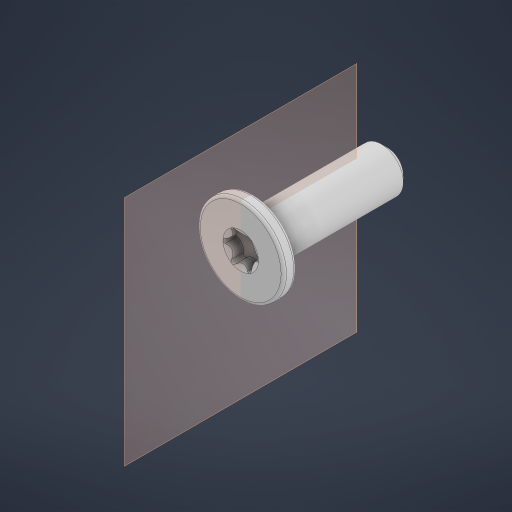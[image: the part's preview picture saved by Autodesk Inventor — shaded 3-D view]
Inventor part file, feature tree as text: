
AUTODESK INVENTOR PART (.ipt)
format: ipt  version: 2024.2 (Build 282272000, 272)  size: 308,224 bytes
history: native  units: in
note: dims shown in document units (in); Inventor stores cm internally (conversion verified against a paired STEP export)
features: other x18, sketch x6, extrude x3, fillet x1, chamfer x1, plane x1, revolve x1
ambient origin geometry x8: Origin, YZ Plane, XZ Plane, XY Plane, X Axis, Y Axis, Z Axis, Center Point
bodies: Solid1 (feature_tree)
feature tree (31):
  other  "Table"
  other  "Screw Steel Flat Head - Star"
  other  "SScrew Star Flat-Head 0.290"
  other  "SScrew Star Flat-Head 0.375"
  other  "SScrew Star Flat-Head 0.500"
  other  "SScrew Star Flat-Head 0.625"
  other  "SScrew Star Flat-Head 0.750"
  other  "SScrew Star Flat-Head 0.875"
  other  "SScrew Star Flat-Head 1.000"
  other  "SScrew Star Flat-Head 1.250"
  other  "SScrew Star Flat-Head 1.375"
  other  "SScrew Star Flat-Head 1.500"
  other  "SScrew Star Flat-Head 1.625"
  other  "SScrew Star Flat-Head 1.750"
  other  "SScrew Star Flat-Head 1.875"
  other  "SScrew Star Flat-Head 2.000"
  other  "SScrew Star Flat-Head 2.250"
  other  "SScrew Star Flat-Head 2.500"
  extrude  "Extrusion1"  Depth=0.047in TaperAngle=0.0deg
  fillet  "Fillet2"  Radius=0.01in
  extrude  "Extrusion2"  TaperAngle=60.0deg  [1 undecoded]
  sketch  "Sketch4"  dims[d8=60.0deg d9=60.0deg]
  sketch  "Sketch6"  dims[d10=0.115in]
  extrude  "Extrusion4"  TaperAngle=60.0deg  [1 undecoded]
  chamfer  "Chamfer1"  Distance=0.017in
  sketch  "Sketch7"  dims[d11=0.017in]
  plane  "Work Plane1"
  revolve  "Revolution2"  [1 undecoded]
  sketch  "Sketch1"  dims[d0=0.321in d1=0.047in d2=0.0in d5=0.01in]
  sketch  "Sketch3"  dims[d6=0.132in d7=60.0deg]
  sketch  "Sketch9"  dims[d12=0.017in d13=0.017in d14=0.017in d15=0.163in d16=30.0deg d17=0.0944in d18=30.0deg d19=30.0deg d20=30.0deg d21=0.0589in d22=0.0in d23=0.164in d24=0.117in d28=0.0in d29=0.0235in d30=0.125in d31=45.0deg d33=0.0089in d34=0.0905in d39=0.035in d40=90.0deg d25=0.0in d26=0.0in]
note: 3 required parameter values undecoded (feature->parameter linkage not recoverable at this tier; creation-order binding heuristic only, values carry confidence <= 0.55)